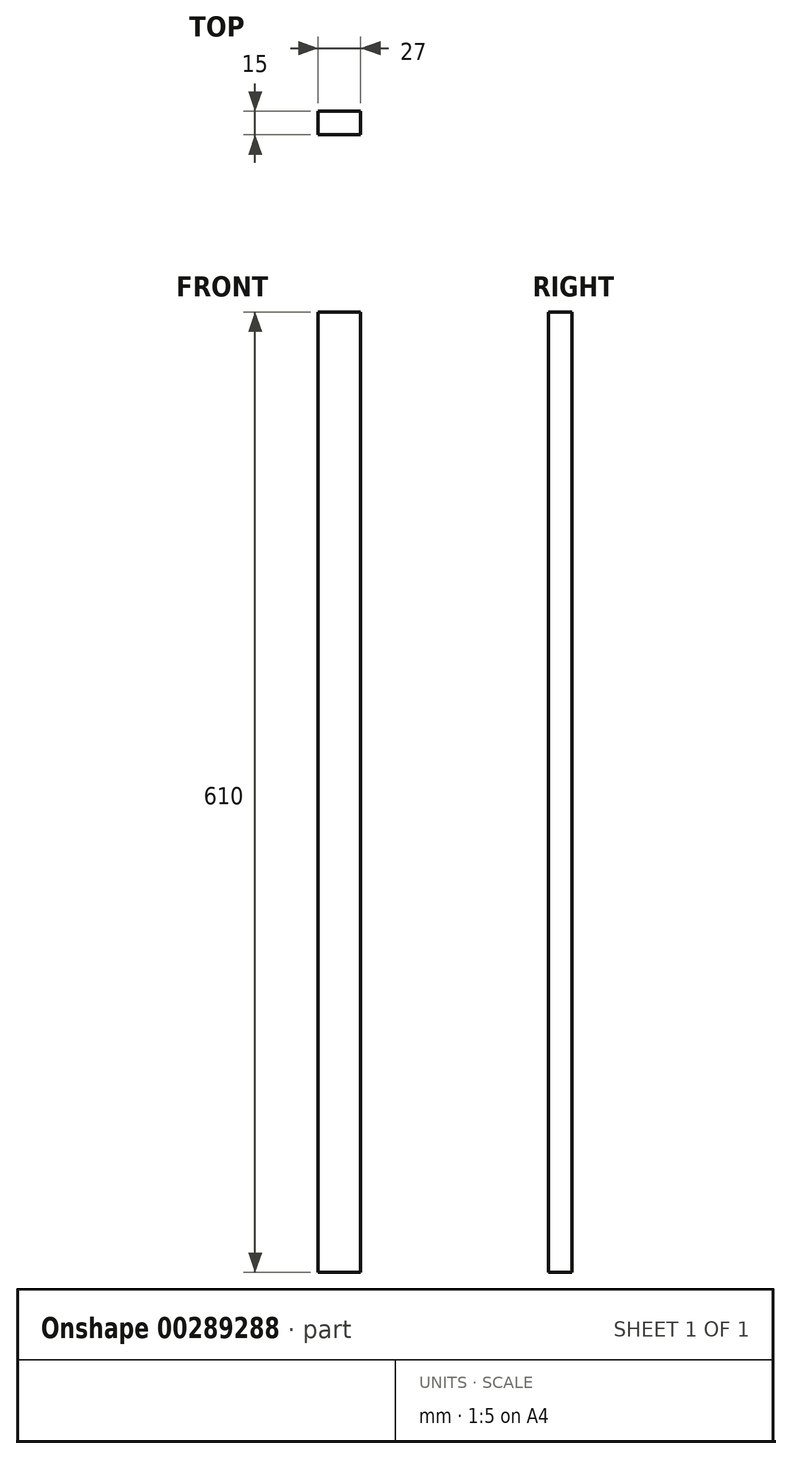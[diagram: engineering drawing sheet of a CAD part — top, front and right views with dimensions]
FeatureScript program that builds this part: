
annotation { "Feature Type Name" : "Feature", "Feature Type Description" : "" }
export const myFeature = defineFeature(function(context is Context, id is Id, definition is map)
    precondition{}
    {
        {
            var Q0;
            Q0=qCreatedBy(makeId("Top.planeOp"),FACE);
            var sketch = newSketch(context, id + "F0", { "sketchPlane" : qUnion([Q0])});
            skLineSegment(sketch, "E0.bottom", {"start": v(0, 0) * mm, "end": v(27, 0) * mm});
            skLineSegment(sketch, "E0.top", {"start": v(0, -15) * mm, "end": v(27, -15) * mm});
            skLineSegment(sketch, "E0.left", {"start": v(0, 0) * mm, "end": v(0, -15) * mm});
            skLineSegment(sketch, "E0.right", {"start": v(27, 0) * mm, "end": v(27, -15) * mm});
            skSolve(sketch);
        }
        {
            var Q0;
            Q0=makeQuery(id+"F0.imprint","IMPRINT",FACE,{"disambiguationData":[TD([[makeQuery(id+"F0.imprint","IMPRINT",EDGE,{"derivedFrom":sQuery(id+"F0.wireOp",EDGE,"E0.bottom")}),-1.0]])]});
            extrude(context, id + "F1", {"entities" : qUnion([Q0]), "depth" : 610 * mm});
        }
    });
